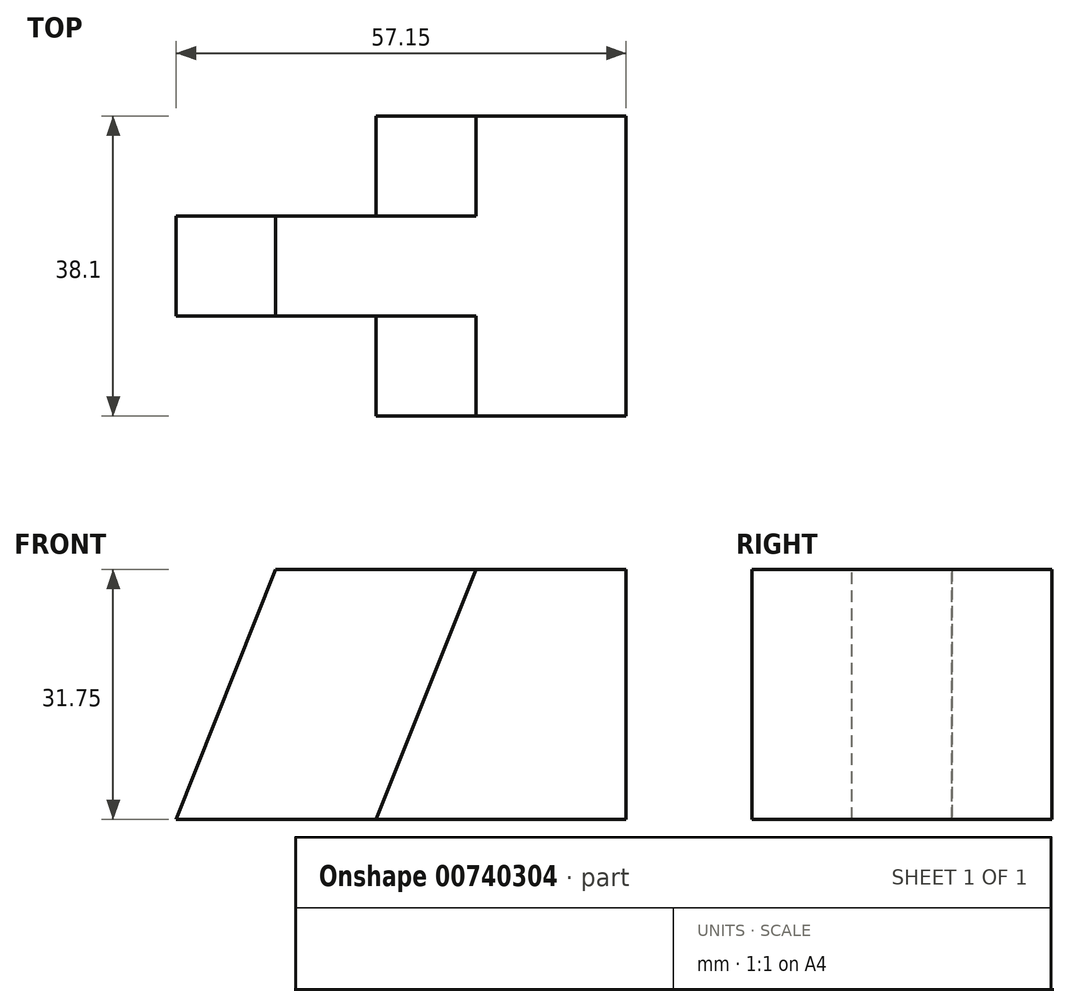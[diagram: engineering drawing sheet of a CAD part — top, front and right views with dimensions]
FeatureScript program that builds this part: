
annotation { "Feature Type Name" : "Feature", "Feature Type Description" : "" }
export const myFeature = defineFeature(function(context is Context, id is Id, definition is map)
    precondition{}
    {
        {
            var Q0;
            Q0=qCreatedBy(makeId("Front.planeOp"),FACE);
            var sketch = newSketch(context, id + "F0", { "sketchPlane" : qUnion([Q0])});
            skLineSegment(sketch, "E0", {"start": v(0, 0) * mm, "end": v(57.15, 0) * mm});
            skLineSegment(sketch, "E1", {"start": v(57.15, 0) * mm, "end": v(57.15, 31.75) * mm});
            skLineSegment(sketch, "E2", {"start": v(57.15, 31.75) * mm, "end": v(0, 31.75) * mm});
            skLineSegment(sketch, "E3", {"start": v(0, 31.75) * mm, "end": v(0, 0) * mm});
            skSolve(sketch);
        }
        {
            var Q0;
            Q0 = qSketchRegion(id + "F0", true);
            extrude(context, id + "F1", {"entities" : qUnion([Q0]), "depth" : 38.1 * mm, "offsetDistance" : 25.4 * mm});
        }
        {
            var Q0;
            Q0=qCreatedBy(makeId("Front.planeOp"),FACE);
            var sketch = newSketch(context, id + "F2", { "sketchPlane" : qUnion([Q0])});
            skLineSegment(sketch, "E4", {"start": v(12.7, 39.36) * mm, "end": v(0, 39.36) * mm});
            skLineSegment(sketch, "E5", {"start": v(12.7, 39.36) * mm, "end": v(12.7, 31.88) * mm});
            skLineSegment(sketch, "E6", {"start": v(12.7, 31.88) * mm, "end": v(0, 0) * mm});
            skLineSegment(sketch, "E7", {"start": v(0, 0) * mm, "end": v(0, 31.88) * mm});
            skLineSegment(sketch, "E8", {"start": v(0, 31.88) * mm, "end": v(12.7, 31.88) * mm});
            skSolve(sketch);
        }
        {
            var Q0;
            Q0=makeQuery(id+"F2.imprint","IMPRINT",FACE,{"disambiguationData":[TD([[makeQuery(id+"F2.imprint","IMPRINT",EDGE,{"derivedFrom":sQuery(id+"F2.wireOp",EDGE,"E6")}),-1.0]])]});
            extrude(context, id + "F3", {"entities" : qUnion([Q0]), "operationType" : NewBodyOperationType.REMOVE, "depth" : 64.77 * mm, "offsetDistance" : 25.4 * mm});
        }
        {
            var Q0;
            Q0=qCreatedBy(makeId("Right.planeOp"),FACE);
            var sketch = newSketch(context, id + "F4", { "sketchPlane" : qUnion([Q0])});
            skLineSegment(sketch, "E9", {"start": v(0, 32.23) * mm, "end": v(-12.7, 32.23) * mm});
            skLineSegment(sketch, "E10", {"start": v(-12.7, 32.23) * mm, "end": v(-38.1, 32.23) * mm});
            skLineSegment(sketch, "E11", {"start": v(-38.1, 32.23) * mm, "end": v(-25.4, 32.23) * mm});
            skLineSegment(sketch, "E12", {"start": v(-12.7, 32.23) * mm, "end": v(-12.7, 0) * mm});
            skLineSegment(sketch, "E13", {"start": v(-12.7, 0) * mm, "end": v(0, 0) * mm});
            skLineSegment(sketch, "E14", {"start": v(0, 0) * mm, "end": v(0, 32.23) * mm});
            skLineSegment(sketch, "E15", {"start": v(-25.4, 32.23) * mm, "end": v(-25.4, 0) * mm});
            skLineSegment(sketch, "E16", {"start": v(-25.4, 0) * mm, "end": v(-38.2, 0) * mm});
            skLineSegment(sketch, "E17", {"start": v(-38.2, 0) * mm, "end": v(-38.1, 32.23) * mm});
            skSolve(sketch);
        }
        {
            var Q0;
            {var subQ2=sQuery(id+"F4.wireOp",EDGE,"E15");Q0=qUnion([makeQuery(id+"F4.imprint","IMPRINT",FACE,{"disambiguationData":[TD([[makeQuery(id+"F4.imprint","IMPRINT",EDGE,{"derivedFrom":sQuery(id+"F4.wireOp",EDGE,"E9")}),1.0]])]}),makeQuery(id+"F4.imprint","IMPRINT",FACE,{"disambiguationData":[TD([[makeQuery(id+"F4.imprint","IMPRINT",EDGE,{"derivedFrom":subQ2}),-1.0]])]})]);}
            extrude(context, id + "F5", {"entities" : qUnion([Q0]), "operationType" : NewBodyOperationType.REMOVE, "depth" : 25.4 * mm, "offsetDistance" : 25.4 * mm});
        }
        {
            var Q0;
            Q0=qCreatedBy(makeId("Front.planeOp"),FACE);
            var sketch = newSketch(context, id + "F6", { "sketchPlane" : qUnion([Q0])});
            skLineSegment(sketch, "E18", {"start": v(25.4, 31.79) * mm, "end": v(38.1, 31.79) * mm});
            skLineSegment(sketch, "E19", {"start": v(38.1, 31.79) * mm, "end": v(25.37, 0) * mm});
            skLineSegment(sketch, "E20", {"start": v(25.37, 0) * mm, "end": v(25.4, 31.79) * mm});
            skSolve(sketch);
        }
        {
            var Q0;
            Q0 = qSketchRegion(id + "F6", true);
            extrude(context, id + "F7", {"entities" : qUnion([Q0]), "operationType" : NewBodyOperationType.REMOVE, "depth" : 12.7 * mm, "offsetDistance" : 25.4 * mm});
        }
        {
            var Q0;
            Q0=qCreatedBy(makeId("Front.planeOp"),FACE);
            var sketch = newSketch(context, id + "F8", { "sketchPlane" : qUnion([Q0])});
            skLineSegment(sketch, "E21", {"start": v(61.15, -53.3) * mm, "end": v(75.16, -53.3) * mm});
            skLineSegment(sketch, "E22", {"start": v(75.16, -53.3) * mm, "end": v(93.44, -96.28) * mm});
            skLineSegment(sketch, "E23", {"start": v(93.44, -96.28) * mm, "end": v(79, -96.28) * mm});
            skLineSegment(sketch, "E24", {"start": v(79, -96.28) * mm, "end": v(79, -128.8) * mm});
            skLineSegment(sketch, "E25", {"start": v(79, -128.8) * mm, "end": v(61.1, -85.58) * mm});
            skLineSegment(sketch, "E26", {"start": v(61.1, -85.58) * mm, "end": v(61.15, -53.3) * mm});
            skLineSegment(sketch, "E27", {"start": v(93.44, -96.28) * mm, "end": v(94.5, -129) * mm});
            skLineSegment(sketch, "E28", {"start": v(94.5, -129) * mm, "end": v(79, -128.8) * mm});
            skSolve(sketch);
        }
        {
            var Q0;
            Q0 = qSketchRegion(id + "F8", true);
            extrude(context, id + "F9", {"entities" : qUnion([Q0]), "operationType" : NewBodyOperationType.REMOVE, "oppositeDirection" : true, "depth" : 12.7 * mm, "offsetDistance" : 25.4 * mm});
        }
        {
            var Q0;
            Q0=makeQuery(id+"F1.opExtrude","CAP_FACE",FACE,{"disambiguationData":[OSD([sQuery(id+"F0.wireOp",EDGE,"E0"),sQuery(id+"F0.wireOp",EDGE,"E1"),sQuery(id+"F0.wireOp",EDGE,"E2"),sQuery(id+"F0.wireOp",EDGE,"E3")])],"isStart":false});
            var sketch = newSketch(context, id + "F10", { "sketchPlane" : qUnion([Q0])});
            skLineSegment(sketch, "E29", {"start": v(38.1, 31.75) * mm, "end": v(25.4, 0) * mm});
            skSolve(sketch);
        }
        {
            var Q0;
            Q0 = qSketchRegion(id + "F10", true);
            var Q1;
            {var subQ0=sQuery(id+"F10.wireOp",EDGE,"E29");Q1=makeQuery(id+"F10.imprint","IMPRINT",FACE,{"disambiguationData":[TD([[makeQuery(id+"F10.imprint","IMPRINT",EDGE,{"derivedFrom":subQ0}),-1.0]])]});}
            extrude(context, id + "F11", {"entities" : qUnion([Q0, Q1]), "operationType" : NewBodyOperationType.REMOVE, "oppositeDirection" : true, "depth" : 12.7 * mm, "offsetDistance" : 25.4 * mm});
        }
    });
